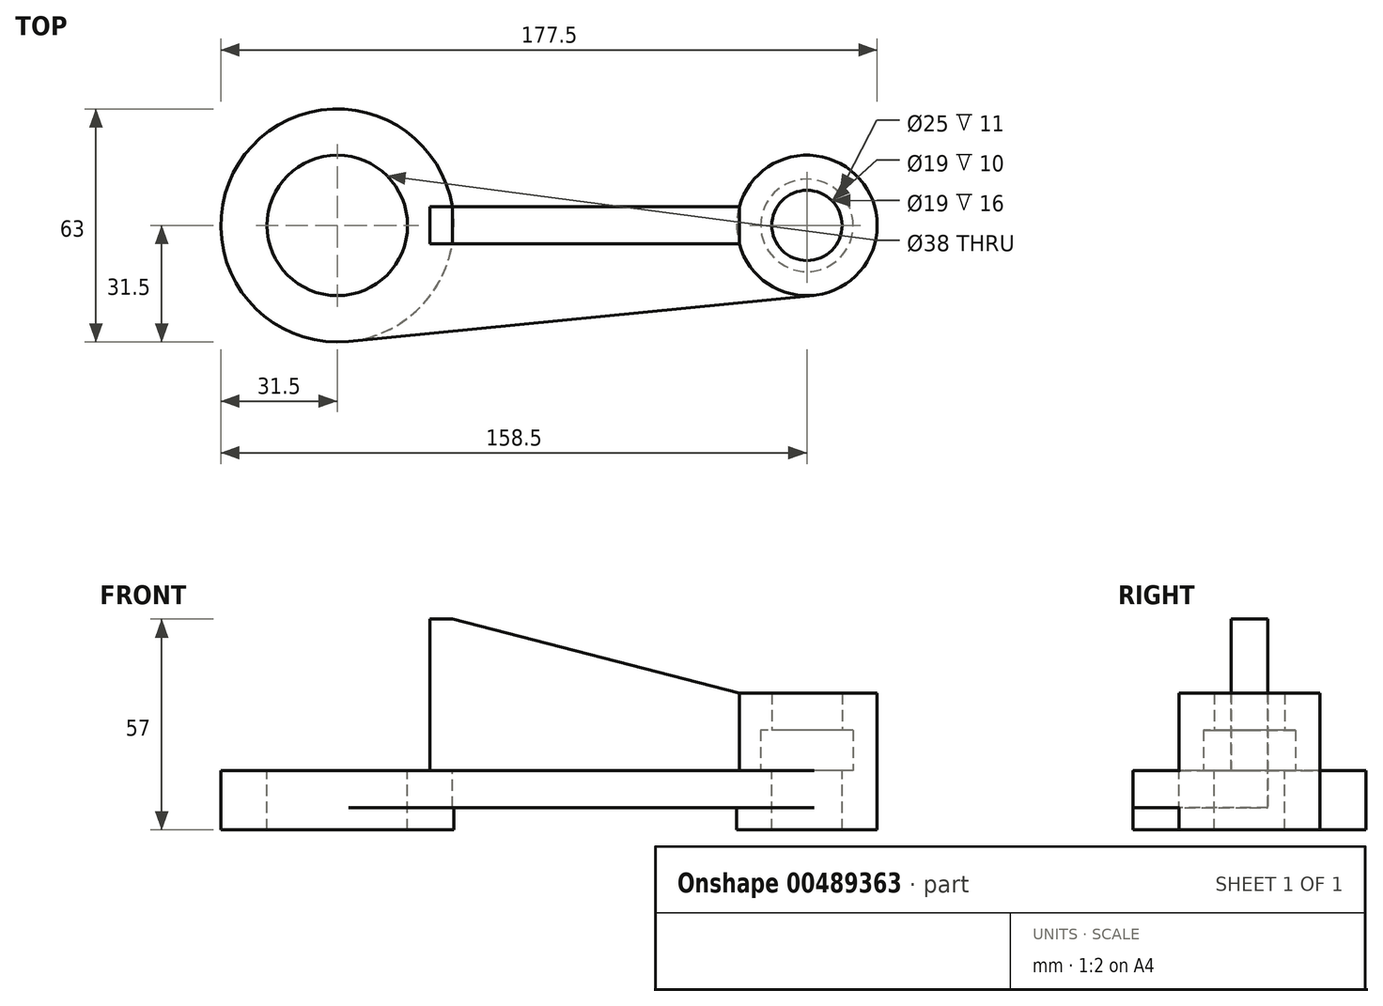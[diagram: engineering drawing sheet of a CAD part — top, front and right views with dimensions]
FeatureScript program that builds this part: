
annotation { "Feature Type Name" : "Feature", "Feature Type Description" : "" }
export const myFeature = defineFeature(function(context is Context, id is Id, definition is map)
    precondition{}
    {
        {
            var Q0;
            Q0=qCreatedBy(makeId("Top.planeOp"),FACE);
            var sketch = newSketch(context, id + "F0", { "sketchPlane" : qUnion([Q0])});
            skCircle(sketch, "E0", {"center": v(0, 0) * mm, "radius": 19 * mm});
            skCircle(sketch, "E1", {"center": v(0, 0) * mm, "radius": 31.5 * mm});
            skLineSegment(sketch, "E2", {"start": v(0, 0) * mm, "end": v(127, 0) * mm, "construction": true});
            skCircle(sketch, "E3", {"center": v(127, 0) * mm, "radius": 12.5 * mm});
            skCircle(sketch, "E4", {"center": v(127, 0) * mm, "radius": 19 * mm});
            skLineSegment(sketch, "E5", {"start": v(31.1, -5) * mm, "end": v(108.67, -5) * mm});
            skLineSegment(sketch, "E6", {"start": v(31.1, 5) * mm, "end": v(108.67, 5) * mm});
            skLineSegment(sketch, "E7", {"start": v(3.1, -31.35) * mm, "end": v(128.87, -18.9) * mm});
            skLineSegment(sketch, "E8", {"start": v(3.1, 31.35) * mm, "end": v(128.87, 18.9) * mm});
            skCircle(sketch, "E9", {"center": v(127, 0) * mm, "radius": 9.5 * mm});
            skSolve(sketch);
        }
        {
            var Q0;
            Q0=makeQuery(id+"F0.imprint","IMPRINT",FACE,{"disambiguationData":[TD([[makeQuery(id+"F0.imprint","IMPRINT",EDGE,{"derivedFrom":sQuery(id+"F0.wireOp",EDGE,"E3")}),-1.0]])]});
            extrude(context, id + "F1", {"entities" : qUnion([Q0]), "depth" : 11 * mm, "offsetDistance" : 25 * mm});
        }
        {
            var Q0;
            Q0=makeQuery(id+"F0.imprint","IMPRINT",FACE,{"disambiguationData":[TD([[makeQuery(id+"F0.imprint","IMPRINT",EDGE,{"derivedFrom":sQuery(id+"F0.wireOp",EDGE,"E0")}),-1.0]])]});
            extrude(context, id + "F2", {"entities" : qUnion([Q0]), "depth" : 41 * mm, "offsetDistance" : 25 * mm});
        }
        {
            var Q0;
            {var subQ0=sQuery(id+"F0.wireOp",EDGE,"E5");Q0=makeQuery(id+"F0.imprint","IMPRINT",FACE,{"disambiguationData":[TD([[makeQuery(id+"F0.imprint","IMPRINT",EDGE,{"derivedFrom":subQ0}),-1.0]])]});}
            var Q1;
            {var subQ0=sQuery(id+"F0.wireOp",EDGE,"E6");Q1=makeQuery(id+"F0.imprint","IMPRINT",FACE,{"disambiguationData":[TD([[makeQuery(id+"F0.imprint","IMPRINT",EDGE,{"derivedFrom":subQ0}),1.0]])]});}
            extrude(context, id + "F3", {"entities" : qUnion([Q0, Q1]), "oppositeDirection" : true, "depth" : 10 * mm, "offsetDistance" : 25 * mm});
        }
        {
            var Q0;
            Q0=makeQuery(id+"F0.imprint","IMPRINT",FACE,{"disambiguationData":[TD([[makeQuery(id+"F0.imprint","IMPRINT",EDGE,{"derivedFrom":sQuery(id+"F0.wireOp",EDGE,"E3")}),1.0]])]});
            var Q1;
            Q1=makeQuery(id+"F0.imprint","IMPRINT",FACE,{"disambiguationData":[TD([[makeQuery(id+"F0.imprint","IMPRINT",EDGE,{"derivedFrom":sQuery(id+"F0.wireOp",EDGE,"E3")}),-1.0]])]});
            extrude(context, id + "F4", {"entities" : qUnion([Q0, Q1]), "operationType" : NewBodyOperationType.INTERSECT, "depth" : 32 * mm, "offsetDistance" : 25 * mm});
        }
        {
            var Q0;
            {var subQ0=sQuery(id+"F0.wireOp",EDGE,"E5");Q0=makeQuery(id+"F0.imprint","IMPRINT",FACE,{"disambiguationData":[TD([[makeQuery(id+"F0.imprint","IMPRINT",EDGE,{"derivedFrom":subQ0}),-1.0]])]});}
            extrude(context, id + "F5", {"entities" : qUnion([Q0]), "oppositeDirection" : true, "depth" : 10 * mm, "offsetDistance" : 25 * mm});
        }
        {
            var Q0;
            Q0=makeQuery(id+"F1.opExtrude","CAP_FACE",FACE,{"disambiguationData":[OSD([sQuery(id+"F0.wireOp",EDGE,"E3"),sQuery(id+"F0.wireOp",EDGE,"E4")])],"isStart":false});
            cPlane(context, id + "F6", {"entities" : qUnion([Q0]), "cplaneType" : CPlaneType.OFFSET, "offset" : 0 * mm, "width" : 150 * mm, "height" : 150 * mm});
        }
        {
            var Q0;
            Q0=qCreatedBy(id+"F6.planeOp",FACE);
            var sketch = newSketch(context, id + "F7", { "sketchPlane" : qUnion([Q0])});
            skPoint(sketch, "E10.0", {"position": v(127, 0) * mm});
            skCircle(sketch, "E11", {"center": v(127, 0) * mm, "radius": 19 * mm});
            skCircle(sketch, "E12", {"center": v(127, 0) * mm, "radius": 9.5 * mm});
            skSolve(sketch);
        }
        {
            var Q0;
            Q0 = qSketchRegion(id + "F7", true);
            extrude(context, id + "F8", {"entities" : qUnion([Q0]), "operationType" : NewBodyOperationType.ADD, "depth" : 10 * mm, "offsetDistance" : 25 * mm});
        }
        {
            var Q0;
            Q0=makeQuery(id+"F0.imprint","IMPRINT",FACE,{"disambiguationData":[TD([[makeQuery(id+"F0.imprint","IMPRINT",EDGE,{"derivedFrom":sQuery(id+"F0.wireOp",EDGE,"E3")}),-1.0]])]});
            var Q1;
            Q1=makeQuery(id+"F0.imprint","IMPRINT",FACE,{"disambiguationData":[TD([[makeQuery(id+"F0.imprint","IMPRINT",EDGE,{"derivedFrom":sQuery(id+"F0.wireOp",EDGE,"E3")}),1.0]])]});
            extrude(context, id + "F9", {"entities" : qUnion([Q0, Q1]), "operationType" : NewBodyOperationType.ADD, "oppositeDirection" : true, "depth" : 16 * mm, "offsetDistance" : 25 * mm});
        }
        {
            var Q0;
            Q0=makeQuery(id+"F0.imprint","IMPRINT",FACE,{"disambiguationData":[TD([[makeQuery(id+"F0.imprint","IMPRINT",EDGE,{"derivedFrom":sQuery(id+"F0.wireOp",EDGE,"E0")}),-1.0]])]});
            extrude(context, id + "F10", {"entities" : qUnion([Q0]), "operationType" : NewBodyOperationType.ADD, "oppositeDirection" : true, "depth" : 16 * mm, "offsetDistance" : 25 * mm});
        }
        {
            var Q0;
            {var subQ0=sQuery(id+"F0.wireOp",EDGE,"E5");Q0=makeQuery(id+"F0.imprint","IMPRINT",FACE,{"disambiguationData":[TD([[makeQuery(id+"F0.imprint","IMPRINT",EDGE,{"derivedFrom":subQ0}),1.0]])]});}
            extrude(context, id + "F11", {"entities" : qUnion([Q0]), "oppositeDirection" : true, "depth" : 10 * mm, "offsetDistance" : 25 * mm});
        }
        {
            var Q0;
            Q0=qCreatedBy(makeId("Right.planeOp"),FACE);
            cPlane(context, id + "F12", {"entities" : qUnion([Q0]), "cplaneType" : CPlaneType.OFFSET, "offset" : 25 * mm, "width" : 150 * mm, "height" : 150 * mm});
        }
        {
            var Q0;
            Q0=qCreatedBy(id+"F12.planeOp",FACE);
            var sketch = newSketch(context, id + "F13", { "sketchPlane" : qUnion([Q0])});
            skPoint(sketch, "E13.0", {"position": v(-5, 0) * mm});
            skPoint(sketch, "E14.0", {"position": v(5, 0) * mm});
            skLineSegment(sketch, "E15.0", {"start": v(-31.5, 41) * mm, "end": v(31.5, 41) * mm});
            skLineSegment(sketch, "E16.bottom", {"start": v(-5, 0) * mm, "end": v(5, 0) * mm});
            skLineSegment(sketch, "E16.top", {"start": v(-5, 41) * mm, "end": v(5, 41) * mm});
            skLineSegment(sketch, "E16.left", {"start": v(-5, 0) * mm, "end": v(-5, 41) * mm});
            skLineSegment(sketch, "E16.right", {"start": v(5, 0) * mm, "end": v(5, 41) * mm});
            skSolve(sketch);
        }
        {
            var Q0;
            Q0=makeQuery(id+"F13.imprint","IMPRINT",FACE,{"disambiguationData":[TD([[makeQuery(id+"F13.imprint","IMPRINT",EDGE,{"derivedFrom":sQuery(id+"F13.wireOp",EDGE,"E16.bottom")}),1.0]])]});
            var Q1;
            Q1=makeQuery(id+"F1.opExtrude","SWEPT_BODY",BODY,{"disambiguationData":[OSD([sQuery(id+"F0.wireOp",EDGE,"E3"),sQuery(id+"F0.wireOp",EDGE,"E4")])]});
            extrude(context, id + "F14", {"entities" : qUnion([Q0]), "operationType" : NewBodyOperationType.ADD, "depth" : 87.1 * mm, "endBoundEntityBody" : qUnion([Q1]), "offsetDistance" : 25 * mm});
        }
        {
            var Q0;
            Q0=makeQuery(id+"F14.opExtrude","SWEPT_FACE",FACE,{"disambiguationData":[OSD([sQuery(id+"F13.wireOp",EDGE,"E16.left")])]});
            var sketch = newSketch(context, id + "F15", { "sketchPlane" : qUnion([Q0])});
            skLineSegment(sketch, "E17.0", {"start": v(108, 21) * mm, "end": v(146, 21) * mm});
            skLineSegment(sketch, "E18.0", {"start": v(112.1, 0) * mm, "end": v(112.1, 41) * mm});
            skPoint(sketch, "E19", {"position": v(108.67, 21) * mm});
            skLineSegment(sketch, "E20", {"start": v(108.67, 21) * mm, "end": v(31.1, 41) * mm});
            skSolve(sketch);
        }
        {
            var Q0;
            Q0 = qSketchRegion(id + "F15", true);
            var Q1;
            {var subQ4=sQuery(id+"F15.wireOp",EDGE,"E20");Q1=makeQuery(id+"F15.imprint","IMPRINT",FACE,{"disambiguationData":[TD([[makeQuery(id+"F15.imprint","IMPRINT",EDGE,{"derivedFrom":subQ4}),-1.0]])]});}
            extrude(context, id + "F16", {"entities" : qUnion([Q0, Q1]), "operationType" : NewBodyOperationType.REMOVE, "oppositeDirection" : true, "depth" : 25 * mm, "offsetDistance" : 25 * mm});
        }
    });
